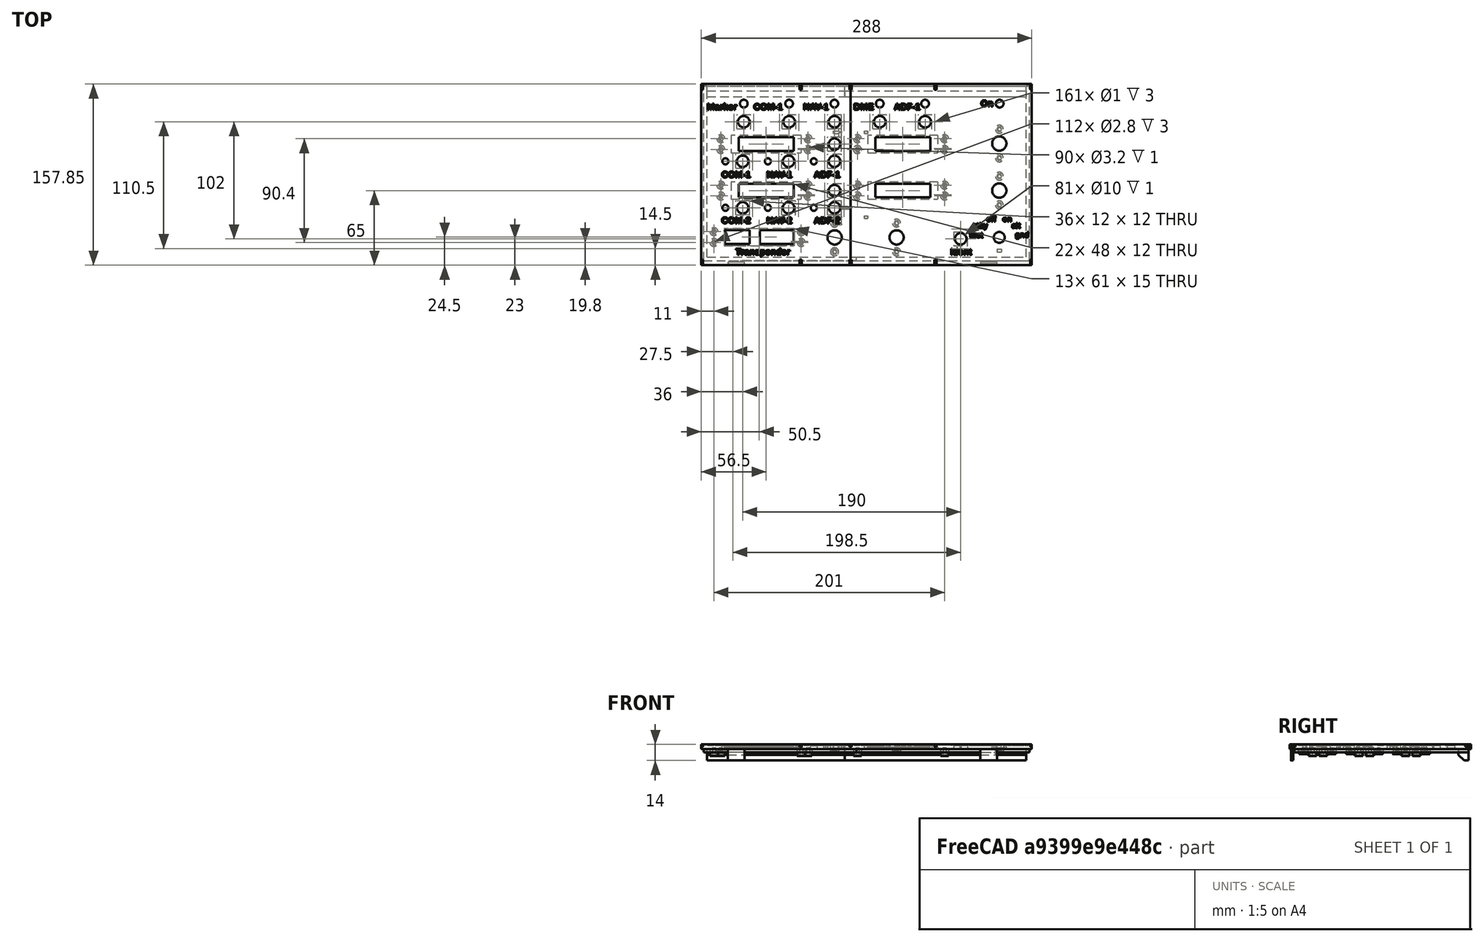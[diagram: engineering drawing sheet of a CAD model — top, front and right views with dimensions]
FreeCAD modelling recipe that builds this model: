
FCSTD DOCUMENT  (FreeCAD 0.17R13522 (Git))
Label: panel_frente_entero
License: CreativeCommons Attribution-ShareAlike
LicenseURL: http://creativecommons.org/licenses/by-sa/4.0/
objects: Part::Feature×33, Part::Cut×28, Part::Box×20, Part::MultiFuse×13, Part::Fuse×6
note: 100 computed .brp shape members not serialized (recipe doc carries the construction recipe); baked Part::Feature solids carry a one-line shape summary decoded from their .brp

FEATURE [Part::Feature] Cut001001001002003001008002002033001001001001001001001002001001002001042002001  label="Cut001001001002003001008002002033001001001001001001001002001001002001042003"
  shape: bbox 163 x 157.9 x 19 mm, 920 faces (baked)
FEATURE [Part::Box] Box  label="apoyo_fleje_lateral"
  AttacherType = Attacher::AttachEngine3D
  Height = 2
  Length = 1.5
  Placement = pos=(129.5,-4,-105) rot=(0,0,1;0rad)
  Width = 5
FEATURE [Part::Feature] Box001  label="apoyo_fleje_lateral001"
  Placement = pos=(129.5,148.85,-105) rot=(0,0,1;0rad)
  shape: bbox 1.5 x 5 x 2 mm, 6 faces (baked)
FEATURE [Part::Feature] Box001001  label="apoyo_fleje_lateral002"
  Placement = pos=(286.5,148.85,-105) rot=(0,0,1;0rad)
  shape: bbox 1.5 x 5 x 2 mm, 6 faces (baked)
FEATURE [Part::Feature] Box001001001  label="apoyo_fleje_lateral003"
  Placement = pos=(286.5,-4,-105) rot=(0,0,1;0rad)
  shape: bbox 1.5 x 5 x 2 mm, 6 faces (baked)
FEATURE [Part::Cut] Cut
  Base = -> Cut001001001002003001008002002033001001001001001001001002001001002001042002001
  Refine = true
  Tool = -> Box001001001
FEATURE [Part::Cut] Cut001001001002003001008002002033001001001001001001001002001001002001042002002
  Base = -> Cut
  Refine = true
  Tool = -> Box001001
FEATURE [Part::Cut] Cut001001001002003001008002002033001001001001001001001002001001002001042002003
  Base = -> Cut001001001002003001008002002033001001001001001001001002001001002001042002002
  Refine = true
  Tool = -> Box
FEATURE [Part::Cut] Cut001001001002003001008002002033001001001001001001001002001001002001042002004
  Base = -> Cut001001001002003001008002002033001001001001001001001002001001002001042002003
  Refine = true
  Tool = -> Box001
FEATURE [Part::Box] Box001001002  label="Cube"
  AttacherType = Attacher::AttachEngine3D
  Height = 2
  Length = 2
  Placement = pos=(203,-4,-105) rot=(0,0,1;0rad)
  Width = 5
FEATURE [Part::Feature] Box001001002001  label="Cube001"
  Placement = pos=(203,148.85,-105) rot=(0,0,1;0rad)
  shape: bbox 2 x 5 x 2 mm, 6 faces (baked)
FEATURE [Part::Cut] Cut001001001002003001008002002033001001001001001001001002001001002001042002005
  Base = -> Cut001001001002003001008002002033001001001001001001001002001001002001042002004
  Refine = true
  Tool = -> Box001001002001
FEATURE [Part::Cut] Cut001001001002003001008002002033001001001001001001001002001001002001042002006
  Base = -> Cut001001001002003001008002002033001001001001001001001002001001002001042002005
  Refine = true
  Tool = -> Box001001002
FEATURE [Part::Feature] Body001  label="cortador_parea_encastres"
  Placement = pos=(141,45,-105) rot=(0.57735,-0.57735,-0.57735;2.0944rad)
  shape: bbox 20 x 15 x 2 mm, 6 faces (baked)
FEATURE [Part::Cut] Cut001001001002003001008002002033001001001001001001001002001001002001042002007
  Base = -> Cut001001001002003001008002002033001001001001001001001002001001002001042002006
  Tool = -> Body001
FEATURE [Part::Feature] Body001001  label="cortador_parea_encastres001"
  Placement = pos=(141,117,-105) rot=(0.57735,-0.57735,-0.57735;2.0944rad)
  shape: bbox 20 x 15 x 2 mm, 6 faces (baked)
FEATURE [Part::Cut] Cut001001001002003001008002002033001001001001001001001002001001002001042002008
  Base = -> Cut001001001002003001008002002033001001001001001001001002001001002001042002007
  Tool = -> Body001001
FEATURE [Part::Feature] Body002  label="encastres001"
  Placement = pos=(244,-2,-126) rot=(0,0,1;0rad)
  shape: bbox 14.6 x 1.8 x 20 mm, 6 faces (baked)
FEATURE [Part::Box] Box001001002002  label="Cube002"
  AttacherType = Attacher::AttachEngine3D
  Height = 17
  Length = 13
  Placement = pos=(245,-14,-124) rot=(0,0,1;0rad)
  Width = 14
FEATURE [Part::Feature] Box001001002002001  label="Cube003"
  Placement = pos=(250,-10,-134) rot=(0,0,1;0rad)
  shape: bbox 13 x 14 x 17 mm, 6 faces (baked)
FEATURE [Part::Cut] Cut001001001002003001008002002033001001001001001001001002001001002001042002009
  Base = -> Cut001001001002003001008002002033001001001001001001001002001001002001042002008
  Tool = -> Box001001002002
FEATURE [Part::Feature] Box001001002002001001  label="Cube004"
  Placement = pos=(238,-10,-134) rot=(0,0,1;0rad)
  shape: bbox 13 x 14 x 17 mm, 6 faces (baked)
FEATURE [Part::MultiFuse] Fusion
  Shapes = -> [Box001001002002001001,Box001001002002001]
FEATURE [Part::Cut] Cut001001001002003001008002002033001001001001001001001002001001002001042002010
  Base = -> Body002
  Placement = pos=(0.1,0,0) rot=(0,0,1;0rad)
  Tool = -> Fusion
FEATURE [Part::MultiFuse] Fusion001  label="panel derecho"
  Shapes = -> [Cut001001001002003001008002002033001001001001001001001002001001002001042002010,Cut001001001002003001008002002033001001001001001001001002001001002001042002009]
FEATURE [Part::Box] Box001001002002001002  label="Cube005"
  AttacherType = Attacher::AttachEngine3D
  Height = 4
  Length = 12
  Placement = pos=(130,25,-107) rot=(0,0,1;0rad)
  Width = 24
FEATURE [Part::Box] Box001001002002001003  label="Cube006"
  AttacherType = Attacher::AttachEngine3D
  Height = 4
  Length = 12
  Placement = pos=(130,98,-107) rot=(0,0,1;0rad)
  Width = 24
FEATURE [Part::MultiFuse] Fusion002
  Shapes = -> [Fusion001,Box001001002002001003]
FEATURE [Part::MultiFuse] Fusion003
  Shapes = -> [Fusion002,Box001001002002001002]
FEATURE [Part::Feature] Fusion003001  label="Fusion004"
  shape: bbox 163 x 157.9 x 14 mm, 945 faces (baked)
FEATURE [Part::Feature] Cut001001001002003001008002002033001001001001001001001002001001002001045001  label="Cut001001001002003001008002002033001001001001001001001002001001002001046"
  shape: bbox 135 x 157.9 x 19 mm, 1304 faces (baked)
FEATURE [Part::Feature] Cut001001001002003001008002002033001001001001001001001002001001002001045002001  label="transponder_part001"
  Placement = pos=(-6,0,0) rot=(0,0,1;0rad)
  shape: bbox 88.15 x 29 x 10 mm, 314 faces (baked)
FEATURE [Part::Box] Box001001002002001004  label="Cube007"
  AttacherType = Attacher::AttachEngine3D
  Height = 100
  Length = 88.15
  Placement = pos=(7,3,-195) rot=(0,0,1;0rad)
  Width = 29
FEATURE [Part::Cut] Cut001001001002003001008002002033001001001001001001001002001001002001045002002
  Base = -> Cut001001001002003001008002002033001001001001001001001002001001002001045001
  Refine = true
  Tool = -> Box001001002002001004
FEATURE [Part::Fuse] Fusion003002
  Base = -> Cut001001001002003001008002002033001001001001001001001002001001002001045002001
  Refine = true
  Tool = -> Cut001001001002003001008002002033001001001001001001001002001001002001045002002
FEATURE [Part::Box] Box001001002002001005  label="Cube008"
  AttacherType = Attacher::AttachEngine3D
  Height = 10
  Length = 10
  Placement = pos=(92.2,6.96,-117) rot=(0,0,1;0rad)
  Width = 24
FEATURE [Part::Cut] Cut001001001002003001008002002033001001001001001001001002001001002001045002003
  Base = -> Fusion003002
  Refine = true
  Tool = -> Box001001002002001005
FEATURE [Part::Box] Box002  label="Cube009"
  AttacherType = Attacher::AttachEngine3D
  Height = 4
  Length = 4
  Placement = pos=(92,2,-107) rot=(0,0,1;0rad)
  Width = 31
FEATURE [Part::Fuse] Fusion003003  label="panel_izquierdo_sin_correr_encoder"
  Base = -> Cut001001001002003001008002002033001001001001001001001002001001002001045002003
  Refine = true
  Tool = -> Box002
FEATURE [Part::Box] Box003  label="Cube010"
  AttacherType = Attacher::AttachEngine3D
  Height = 10
  Length = 14
  Placement = pos=(115,10,-109) rot=(0,0,1;0rad)
  Width = 20
FEATURE [Part::Cut] Cut001001001002003001008002002033001001001001001001001002001001002001045002004
  Base = -> Fusion003003
  Refine = true
  Tool = -> Box003
FEATURE [Part::Box] Box004  label="Cube011"
  AttacherType = Attacher::AttachEngine3D
  Height = 10
  Length = 10
  Placement = pos=(117,4,-117) rot=(0,0,1;0rad)
  Width = 10
FEATURE [Part::Feature] Box004001  label="Cube012"
  Placement = pos=(117,28,-117) rot=(0,0,1;0rad)
  shape: bbox 10 x 10 x 10 mm, 6 faces (baked)
FEATURE [Part::Cut] Cut001001001002003001008002002033001001001001001001001002001001002001045002005
  Base = -> Cut001001001002003001008002002033001001001001001001001002001001002001045002004
  Refine = true
  Tool = -> Box004
FEATURE [Part::Cut] Cut001001001002003001008002002033001001001001001001001002001001002001045002006
  Base = -> Cut001001001002003001008002002033001001001001001001001002001001002001045002005
  Refine = true
  Tool = -> Box004001
FEATURE [Part::Box] Box004002  label="Cube013"
  AttacherType = Attacher::AttachEngine3D
  Height = 1
  Length = 5
  Placement = pos=(119,5,-107) rot=(0,0,1;0rad)
  Width = 5
FEATURE [Part::Feature] Box004002001  label="Cube014"
  Placement = pos=(119,31,-107) rot=(0,0,1;0rad)
  shape: bbox 5 x 5 x 1 mm, 6 faces (baked)
FEATURE [Part::Fuse] Fusion003004
  Base = -> Cut001001001002003001008002002033001001001001001001001002001001002001045002006
  Refine = true
  Tool = -> Box004002001
FEATURE [Part::Fuse] Fusion003005
  Base = -> Box004002
  Refine = true
  Tool = -> Fusion003004
FEATURE [Part::Feature] Cut001001001002003001008002002033001001001001001001001002001001002001045002003002  label="doble_cncoder_tra12_soportes001"
  Placement = pos=(-6,0,0) rot=(0,0,1;0rad)
  shape: bbox 22 x 44 x 8.5 mm, 39 faces (baked)
FEATURE [Part::Box] Box004002002  label="Cube015"
  AttacherType = Attacher::AttachEngine3D
  Height = 10
  Length = 18
  Placement = pos=(107,10,-109) rot=(0,0,1;0rad)
  Width = 20
FEATURE [Part::Cut] Cut001001001002003001008002002033001001001001001001001002001001002001045002003003
  Base = -> Fusion003005
  Refine = true
  Tool = -> Box004002002
FEATURE [Part::Fuse] Fusion004  label="Fusion003006"
  Base = -> Cut001001001002003001008002002033001001001001001001001002001001002001045002003002
  Refine = true
  Tool = -> Cut001001001002003001008002002033001001001001001001001002001001002001045002003003
FEATURE [Part::Box] Box004002003  label="Cube016"
  AttacherType = Attacher::AttachEngine3D
  Height = 4
  Length = 6
  Placement = pos=(123,8,-107) rot=(0,0,1;0rad)
  Width = 24
FEATURE [Part::Fuse] Fusion005  label="panel_izquierdo_sin_apya_flejes"
  Base = -> Fusion004
  Refine = true
  Tool = -> Box004002003
FEATURE [Part::Box] Box004002004  label="apoya_fleje_lateral_1"
  AttacherType = Attacher::AttachEngine3D
  Height = 2
  Length = 1.5
  Placement = pos=(0,-4,-105) rot=(0,0,1;0rad)
  Width = 5
FEATURE [Part::Feature] Box004002004001  label="apoya_fleje_lateral_002"
  Placement = pos=(0,148.85,-105) rot=(0,0,1;0rad)
  shape: bbox 1.5 x 5 x 2 mm, 6 faces (baked)
FEATURE [Part::Feature] Box004002004001001  label="apoya_fleje_lateral_003"
  Placement = pos=(85.5,148.85,-105) rot=(0,0,1;0rad)
  shape: bbox 1.5 x 5 x 2 mm, 6 faces (baked)
FEATURE [Part::Feature] Box004002004001001001  label="apoya_fleje_lateral_004"
  Placement = pos=(86,148.85,-105) rot=(0,0,1;0rad)
  shape: bbox 1.5 x 5 x 2 mm, 6 faces (baked)
FEATURE [Part::Feature] Box004002004001001001001  label="apoya_fleje_lateral_005"
  Placement = pos=(129,148.85,-105) rot=(0,0,1;0rad)
  shape: bbox 1.5 x 5 x 2 mm, 6 faces (baked)
FEATURE [Part::Feature] Box004002004001001001002  label="apoya_fleje_lateral_006"
  Placement = pos=(85.5,-4,-105) rot=(0,0,1;0rad)
  shape: bbox 1.5 x 5 x 2 mm, 6 faces (baked)
FEATURE [Part::Feature] Box004002004001001001002001  label="apoya_fleje_lateral_007"
  Placement = pos=(86,-4,-105) rot=(0,0,1;0rad)
  shape: bbox 1.5 x 5 x 2 mm, 6 faces (baked)
FEATURE [Part::Feature] Box004002004001001001002001001  label="apoya_fleje_lateral_008"
  Placement = pos=(129,-4,-105) rot=(0,0,1;0rad)
  shape: bbox 1.5 x 5 x 2 mm, 6 faces (baked)
FEATURE [Part::Cut] Cut001001001002003001008002002033001001001001001001001002001001002001045002003004
  Base = -> Fusion005
  Refine = true
  Tool = -> Box004002004
FEATURE [Part::Cut] Cut001001001002003001008002002033001001001001001001001002001001002001045002003005
  Base = -> Cut001001001002003001008002002033001001001001001001001002001001002001045002003004
  Refine = true
  Tool = -> Box004002004001
FEATURE [Part::Cut] Cut001001001002003001008002002033001001001001001001001002001001002001045002003006
  Base = -> Cut001001001002003001008002002033001001001001001001001002001001002001045002003005
  Refine = true
  Tool = -> Box004002004001001
FEATURE [Part::Cut] Cut001001001002003001008002002033001001001001001001001002001001002001045002003007
  Base = -> Cut001001001002003001008002002033001001001001001001001002001001002001045002003006
  Refine = true
  Tool = -> Box004002004001001001
FEATURE [Part::Cut] Cut001001001002003001008002002033001001001001001001001002001001002001045002003008
  Base = -> Cut001001001002003001008002002033001001001001001001001002001001002001045002003007
  Refine = true
  Tool = -> Box004002004001001001001
FEATURE [Part::Cut] Cut001001001002003001008002002033001001001001001001001002001001002001045002003009
  Base = -> Cut001001001002003001008002002033001001001001001001001002001001002001045002003008
  Refine = true
  Tool = -> Box004002004001001001002
FEATURE [Part::Cut] Cut001001001002003001008002002033001001001001001001001002001001002001045002003010
  Base = -> Cut001001001002003001008002002033001001001001001001001002001001002001045002003009
  Refine = true
  Tool = -> Box004002004001001001002001
FEATURE [Part::Cut] Cut001001001002003001008002002033001001001001001001001002001001002001045002003011
  Base = -> Cut001001001002003001008002002033001001001001001001001002001001002001045002003010
  Refine = true
  Tool = -> Box004002004001001001002001001
FEATURE [Part::Feature] Body001002  label="cortador_parea_encastres002"
  Placement = pos=(120,32,-105) rot=(0.57735,0.57735,0.57735;2.0944rad)
  shape: bbox 20 x 15 x 2 mm, 6 faces (baked)
FEATURE [Part::Feature] Body001003  label="cortador_parea_encastres003"
  Placement = pos=(120,104,-105) rot=(0.57735,0.57735,0.57735;2.0944rad)
  shape: bbox 20 x 15 x 2 mm, 6 faces (baked)
FEATURE [Part::Cut] Cut001001001002003001008002002033001001001001001001001002001001002001045002003012
  Base = -> Cut001001001002003001008002002033001001001001001001001002001001002001045002003011
  Tool = -> Body001002
FEATURE [Part::Cut] Cut001001001002003001008002002033001001001001001001001002001001002001045002003013
  Base = -> Cut001001001002003001008002002033001001001001001001001002001001002001045002003012
  Tool = -> Body001003
FEATURE [Part::Feature] Body001004  label="encastres002"
  Placement = pos=(24.1,-2,-123) rot=(0,0,1;0rad)
  shape: bbox 14.6 x 1.8 x 20 mm, 6 faces (baked)
FEATURE [Part::Box] Box004002004001001001002001002  label="Cube017"
  AttacherType = Attacher::AttachEngine3D
  Height = 19
  Length = 10
  Placement = pos=(24,-7,-126) rot=(0,0,1;0rad)
  Width = 7
FEATURE [Part::Feature] Box004002004001001001002001002001  label="Cube018"
  Placement = pos=(32,-7,-136) rot=(0,0,1;0rad)
  shape: bbox 10 x 7 x 19 mm, 6 faces (baked)
FEATURE [Part::Cut] Cut001001001002003001008002002033001001001001001001001002001001002001045002003014
  Base = -> Cut001001001002003001008002002033001001001001001001001002001001002001045002003013
  Tool = -> Box004002004001001001002001002
FEATURE [Part::Feature] Box004002004001001001002001002001001  label="Cube019"
  Placement = pos=(22,-7,-136) rot=(0,0,1;0rad)
  shape: bbox 10 x 7 x 19 mm, 6 faces (baked)
FEATURE [Part::MultiFuse] Fusion006
  Shapes = -> [Box004002004001001001002001002001,Box004002004001001001002001002001001]
FEATURE [Part::Cut] Cut001001001002003001008002002033001001001001001001001002001001002001045002003015
  Base = -> Body001004
  Tool = -> Fusion006
FEATURE [Part::MultiFuse] Fusion007  label="panel izq"
  Shapes = -> [Cut001001001002003001008002002033001001001001001001001002001001002001045002003014,Cut001001001002003001008002002033001001001001001001001002001001002001045002003015]
FEATURE [Part::Box] Box004002004001001001002001002001002  label="Cube020"
  AttacherType = Attacher::AttachEngine3D
  Height = 4
  Length = 8
  Placement = pos=(122,102,-107) rot=(0,0,1;0rad)
  Width = 17
FEATURE [Part::Box] Box004002004001001001002001002001003  label="Cube021"
  AttacherType = Attacher::AttachEngine3D
  Height = 4
  Length = 8
  Placement = pos=(122,28,-107) rot=(0,0,1;0rad)
  Width = 17
FEATURE [Part::MultiFuse] Fusion008
  Shapes = -> [Fusion007,Box004002004001001001002001002001003]
FEATURE [Part::MultiFuse] Fusion009
  Shapes = -> [Fusion008,Box004002004001001001002001002001002]
FEATURE [Part::Feature] Fusion009001  label="Fusion010"
  shape: bbox 135 x 157.9 x 14 mm, 1338 faces (baked)
FEATURE [Part::Box] Box004002004001001001002001002001004  label="Cube022"
  AttacherType = Attacher::AttachEngine3D
  Height = 4
  Length = 5
  Placement = pos=(125,42,-107) rot=(0,0,1;0rad)
  Width = 6
FEATURE [Part::MultiFuse] Fusion009002
  Shapes = -> [Box004002004001001001002001002001004,Fusion009001]
FEATURE [Part::Feature] Fusion009002001  label="Fusion009003"
  shape: bbox 135 x 157.9 x 14 mm, 1339 faces (baked)
FEATURE [Part::MultiFuse] Fusion009002002
  Shapes = -> [Fusion009002001,Fusion003001]
FEATURE [Part::Feature] Fusion009002002001  label="Fusion009002003"
  shape: bbox 288 x 157.9 x 14 mm, 2272 faces (baked)
FEATURE [Part::MultiFuse] Fusion009002002002
  Shapes = -> [Cut001001001002003001008002002033001001001001001001001002001001002001045002003014,Fusion009002002001]
FEATURE [Part::Feature] Fusion009002002002001  label="Fusion009002002003"
  shape: bbox 288 x 157.9 x 14 mm, 2272 faces (baked)
FEATURE [Part::Box] Box004002004001001001002001002001005  label="Cube023"
  AttacherType = Attacher::AttachEngine3D
  Height = 2
  Length = 288
  Placement = pos=(0,-4,-105) rot=(0,0,1;0rad)
  Width = 6
FEATURE [Part::Box] Box004002004001001001002001002001006  label="Cube024"
  AttacherType = Attacher::AttachEngine3D
  Height = 2
  Length = 288
  Placement = pos=(0,147.85,-105) rot=(0,0,1;0rad)
  Width = 6
FEATURE [Part::MultiFuse] Fusion009002002002002
  Shapes = -> [Fusion009002002002001,Box004002004001001001002001002001006]
FEATURE [Part::MultiFuse] Fusion009002002002003
  Shapes = -> [Box004002004001001001002001002001005,Fusion009002002002002]
FEATURE [Part::Feature] Fusion009002002002003001  label="Fusion009002002002004"
  shape: bbox 288 x 157.9 x 14 mm, 2236 faces (baked)
